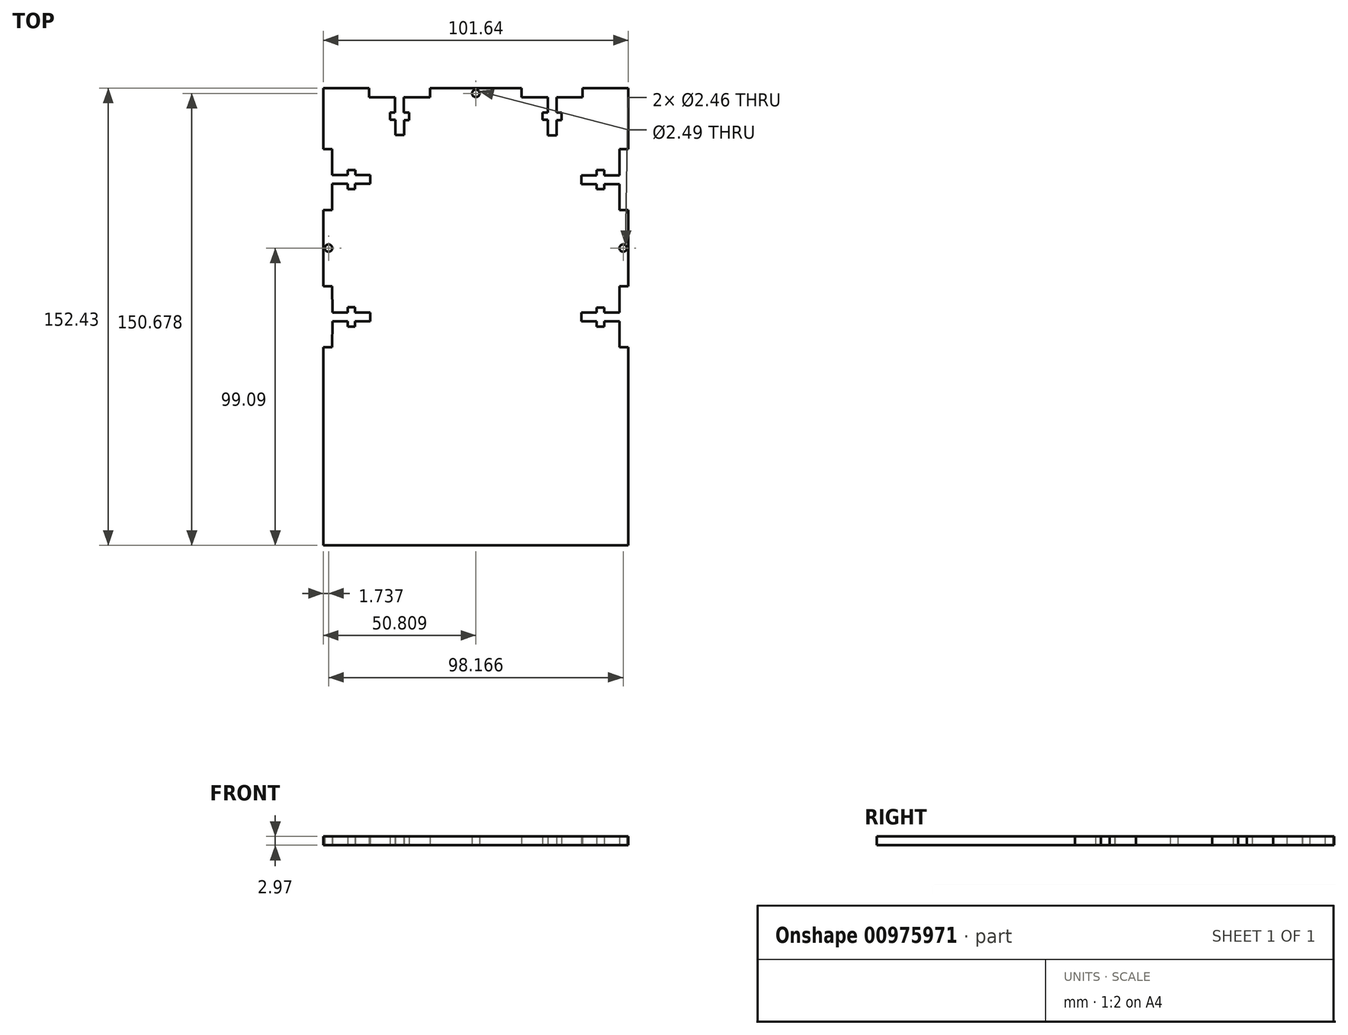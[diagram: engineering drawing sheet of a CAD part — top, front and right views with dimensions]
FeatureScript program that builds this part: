
annotation { "Feature Type Name" : "Feature", "Feature Type Description" : "" }
export const myFeature = defineFeature(function(context is Context, id is Id, definition is map)
    precondition{}
    {
        {
            var Q0;
            Q0=qCreatedBy(makeId("Top.planeOp"),FACE);
            var sketch = newSketch(context, id + "F0", { "sketchPlane" : qUnion([Q0])});
            skLineSegment(sketch, "E0.top", {"start": v(50.82, -76.2) * mm, "end": v(-50.82, -76.2) * mm});
            skPoint(sketch, "E0.middle", {"position": v(0, 0) * mm});
            skPoint(sketch, "E1", {"position": v(-0.02, 76.23) * mm});
            skPoint(sketch, "E2", {"position": v(0, -76.2) * mm});
            skLineSegment(sketch, "E3", {"start": v(-50.82, 76.2) * mm, "end": v(-35.58, 76.2) * mm});
            skLineSegment(sketch, "E4", {"start": v(-0.02, 76.23) * mm, "end": v(-15.26, 76.23) * mm});
            skLineSegment(sketch, "E5", {"start": v(-0.02, 76.23) * mm, "end": v(15.22, 76.23) * mm});
            skLineSegment(sketch, "E6", {"start": v(35.58, 76.2) * mm, "end": v(50.82, 76.2) * mm});
            skLineSegment(sketch, "E7", {"start": v(-50.82, 55.88) * mm, "end": v(-50.82, 76.2) * mm});
            skLineSegment(sketch, "E8", {"start": v(-50.82, 35.56) * mm, "end": v(-50.82, 10.16) * mm});
            skLineSegment(sketch, "E9", {"start": v(-50.82, -10.16) * mm, "end": v(-50.82, -76.2) * mm});
            skLineSegment(sketch, "E10", {"start": v(50.82, -76.2) * mm, "end": v(50.82, -10.16) * mm});
            skLineSegment(sketch, "E11", {"start": v(50.82, 10.16) * mm, "end": v(50.82, 35.56) * mm});
            skLineSegment(sketch, "E12", {"start": v(50.82, 55.88) * mm, "end": v(50.82, 76.2) * mm});
            skLineSegment(sketch, "E13", {"start": v(-50.82, 10.16) * mm, "end": v(-47.85, 10.16) * mm});
            skLineSegment(sketch, "E14", {"start": v(-50.82, -10.16) * mm, "end": v(-47.85, -10.16) * mm});
            skLineSegment(sketch, "E15", {"start": v(-50.82, 55.88) * mm, "end": v(-47.85, 55.88) * mm});
            skLineSegment(sketch, "E16", {"start": v(-50.82, 35.56) * mm, "end": v(-47.85, 35.56) * mm});
            skLineSegment(sketch, "E17", {"start": v(-35.58, 76.2) * mm, "end": v(-35.58, 73.23) * mm});
            skLineSegment(sketch, "E18", {"start": v(-15.26, 76.23) * mm, "end": v(-15.26, 73.23) * mm});
            skLineSegment(sketch, "E19", {"start": v(15.22, 76.23) * mm, "end": v(15.22, 73.23) * mm});
            skLineSegment(sketch, "E20", {"start": v(35.58, 76.2) * mm, "end": v(35.58, 73.23) * mm});
            skLineSegment(sketch, "E21", {"start": v(50.82, 55.88) * mm, "end": v(47.85, 55.88) * mm});
            skLineSegment(sketch, "E22", {"start": v(50.82, 35.56) * mm, "end": v(47.85, 35.56) * mm});
            skLineSegment(sketch, "E23", {"start": v(50.82, 10.16) * mm, "end": v(47.85, 10.16) * mm});
            skLineSegment(sketch, "E24", {"start": v(50.82, -10.16) * mm, "end": v(47.85, -10.16) * mm});
            skLineSegment(sketch, "E25.MirrorCS", {"start": v(-35.15, 45.76) * mm, "end": v(-35.15, 44.3) * mm});
            skLineSegment(sketch, "E26", {"start": v(-47.85, 47.2) * mm, "end": v(-47.85, 55.88) * mm});
            skLineSegment(sketch, "E27", {"start": v(-47.85, 44.3) * mm, "end": v(-47.85, 35.56) * mm});
            skLineSegment(sketch, "E28.bottom", {"start": v(-42.73, 48.94) * mm, "end": v(-40.19, 48.94) * mm});
            skLineSegment(sketch, "E28.top", {"start": v(-42.73, 42.57) * mm, "end": v(-40.26, 42.57) * mm});
            skLineSegment(sketch, "E29", {"start": v(-47.85, 47.2) * mm, "end": v(-42.73, 47.2) * mm});
            skLineSegment(sketch, "E30", {"start": v(-47.85, 44.3) * mm, "end": v(-42.73, 44.3) * mm});
            skLineSegment(sketch, "E31", {"start": v(-35.15, 44.3) * mm, "end": v(-40.26, 44.3) * mm});
            skLineSegment(sketch, "E32", {"start": v(-40.19, 48.94) * mm, "end": v(-40.19, 47.2) * mm});
            skLineSegment(sketch, "E33", {"start": v(-40.26, 44.3) * mm, "end": v(-40.26, 42.57) * mm});
            skLineSegment(sketch, "E34", {"start": v(-42.73, 42.57) * mm, "end": v(-42.73, 44.3) * mm});
            skLineSegment(sketch, "E35", {"start": v(-42.73, 47.2) * mm, "end": v(-42.73, 48.94) * mm});
            skPoint(sketch, "E36", {"position": v(-50.82, 22.86) * mm});
            skLineSegment(sketch, "E37", {"start": v(-25.42, 60.56) * mm, "end": v(-23.96, 60.56) * mm});
            skLineSegment(sketch, "E38.left", {"start": v(-28.6, 68.12) * mm, "end": v(-28.6, 65.66) * mm});
            skLineSegment(sketch, "E38.right", {"start": v(-22.24, 68.12) * mm, "end": v(-22.24, 65.58) * mm});
            skLineSegment(sketch, "E39", {"start": v(-26.88, 73.24) * mm, "end": v(-26.88, 68.12) * mm});
            skLineSegment(sketch, "E40", {"start": v(-23.97, 73.23) * mm, "end": v(-23.97, 68.12) * mm});
            skLineSegment(sketch, "E41", {"start": v(-23.96, 60.56) * mm, "end": v(-23.96, 65.58) * mm});
            skLineSegment(sketch, "E42", {"start": v(-28.6, 68.12) * mm, "end": v(-26.88, 68.12) * mm});
            skLineSegment(sketch, "E43", {"start": v(-23.97, 68.12) * mm, "end": v(-22.24, 68.12) * mm});
            skLineSegment(sketch, "E44", {"start": v(-22.24, 65.58) * mm, "end": v(-23.96, 65.58) * mm});
            skLineSegment(sketch, "E45", {"start": v(-26.88, 65.66) * mm, "end": v(-28.6, 65.66) * mm});
            skLineSegment(sketch, "E46", {"start": v(-35.58, 73.23) * mm, "end": v(-26.88, 73.24) * mm});
            skLineSegment(sketch, "E47", {"start": v(-23.97, 73.23) * mm, "end": v(-15.26, 73.23) * mm});
            skLineSegment(sketch, "E48.MirrorCS", {"start": v(23.92, 68.1) * mm, "end": v(22.2, 68.1) * mm});
            skLineSegment(sketch, "E49.MirrorCS", {"start": v(28.56, 68.12) * mm, "end": v(26.88, 68.12) * mm});
            skLineSegment(sketch, "E50.MirrorCS", {"start": v(26.84, 65.58) * mm, "end": v(28.56, 65.58) * mm});
            skLineSegment(sketch, "E51.MirrorCS", {"start": v(22.2, 65.64) * mm, "end": v(23.92, 65.64) * mm});
            skLineSegment(sketch, "E52.MirrorCS", {"start": v(25.38, 60.53) * mm, "end": v(23.92, 60.53) * mm});
            skLineSegment(sketch, "E53.MirrorCS", {"start": v(23.92, 60.53) * mm, "end": v(23.92, 65.64) * mm});
            skLineSegment(sketch, "E54.MirrorCS", {"start": v(22.2, 68.1) * mm, "end": v(22.2, 65.64) * mm});
            skLineSegment(sketch, "E55.MirrorCS", {"start": v(26.88, 73.24) * mm, "end": v(26.88, 68.12) * mm});
            skLineSegment(sketch, "E56.MirrorCS", {"start": v(23.92, 73.23) * mm, "end": v(23.92, 68.1) * mm});
            skLineSegment(sketch, "E57.MirrorCS", {"start": v(28.56, 68.12) * mm, "end": v(28.56, 65.58) * mm});
            skLineSegment(sketch, "E58", {"start": v(15.22, 73.23) * mm, "end": v(23.92, 73.23) * mm});
            skLineSegment(sketch, "E59", {"start": v(26.88, 73.24) * mm, "end": v(35.58, 73.23) * mm});
            skLineSegment(sketch, "E60.bottom", {"start": v(40.28, 42.59) * mm, "end": v(42.82, 42.59) * mm});
            skLineSegment(sketch, "E60.top", {"start": v(40.28, 48.93) * mm, "end": v(42.74, 48.93) * mm});
            skLineSegment(sketch, "E61", {"start": v(35.15, 44.26) * mm, "end": v(40.28, 44.26) * mm});
            skLineSegment(sketch, "E62", {"start": v(47.85, 44.26) * mm, "end": v(42.82, 44.26) * mm});
            skLineSegment(sketch, "E63", {"start": v(47.85, 47.18) * mm, "end": v(42.74, 47.18) * mm});
            skLineSegment(sketch, "E64", {"start": v(40.28, 47.18) * mm, "end": v(40.28, 48.93) * mm});
            skLineSegment(sketch, "E65", {"start": v(40.28, 44.26) * mm, "end": v(40.28, 42.59) * mm});
            skLineSegment(sketch, "E66", {"start": v(42.82, 42.59) * mm, "end": v(42.82, 44.26) * mm});
            skLineSegment(sketch, "E67", {"start": v(42.74, 47.18) * mm, "end": v(42.74, 48.93) * mm});
            skLineSegment(sketch, "E68", {"start": v(47.85, 47.18) * mm, "end": v(47.85, 55.88) * mm});
            skLineSegment(sketch, "E69", {"start": v(47.85, 44.26) * mm, "end": v(47.85, 35.56) * mm});
            skPoint(sketch, "E70", {"position": v(50.82, 22.86) * mm});
            skLineSegment(sketch, "E71.MirrorCS", {"start": v(42.82, 3.14) * mm, "end": v(42.82, 1.46) * mm});
            skLineSegment(sketch, "E72.MirrorCS", {"start": v(35.15, 0) * mm, "end": v(35.15, 1.46) * mm});
            skLineSegment(sketch, "E73.MirrorCS", {"start": v(40.28, 1.46) * mm, "end": v(40.28, 3.14) * mm});
            skLineSegment(sketch, "E74.MirrorCS", {"start": v(35.15, 0) * mm, "end": v(35.15, -1.46) * mm});
            skLineSegment(sketch, "E75.MirrorCS", {"start": v(40.28, -1.46) * mm, "end": v(40.28, -3.21) * mm});
            skLineSegment(sketch, "E76.MirrorCS", {"start": v(35.15, -1.46) * mm, "end": v(40.28, -1.46) * mm});
            skLineSegment(sketch, "E77.MirrorCS", {"start": v(35.15, 1.46) * mm, "end": v(40.28, 1.46) * mm});
            skLineSegment(sketch, "E78.MirrorCS", {"start": v(40.28, 3.14) * mm, "end": v(42.82, 3.14) * mm});
            skLineSegment(sketch, "E79.MirrorCS", {"start": v(40.28, -3.21) * mm, "end": v(42.74, -3.21) * mm});
            skLineSegment(sketch, "E80.MirrorCS", {"start": v(47.85, -1.46) * mm, "end": v(42.74, -1.46) * mm});
            skLineSegment(sketch, "E81", {"start": v(47.85, 1.46) * mm, "end": v(47.85, 10.16) * mm});
            skLineSegment(sketch, "E82", {"start": v(47.85, -1.46) * mm, "end": v(47.85, -10.16) * mm});
            skLineSegment(sketch, "E83.MirrorCS", {"start": v(-40.26, 1.43) * mm, "end": v(-40.26, 3.16) * mm});
            skLineSegment(sketch, "E84.MirrorCS", {"start": v(-35.15, -0.03) * mm, "end": v(-35.15, 1.43) * mm});
            skLineSegment(sketch, "E85.MirrorCS", {"start": v(-35.15, 1.43) * mm, "end": v(-40.26, 1.43) * mm});
            skLineSegment(sketch, "E86.MirrorCS", {"start": v(-42.72, -1.5) * mm, "end": v(-42.72, -3.22) * mm});
            skLineSegment(sketch, "E87.MirrorCS", {"start": v(-35.15, -0.03) * mm, "end": v(-35.15, -1.5) * mm});
            skLineSegment(sketch, "E88.MirrorCS", {"start": v(-35.15, -1.5) * mm, "end": v(-40.26, -1.5) * mm});
            skLineSegment(sketch, "E89.MirrorCS", {"start": v(-42.72, -3.22) * mm, "end": v(-40.26, -3.22) * mm});
            skLineSegment(sketch, "E90.MirrorCS", {"start": v(-42.72, 3.16) * mm, "end": v(-40.26, 3.16) * mm});
            skLineSegment(sketch, "E91.MirrorCS", {"start": v(-42.72, 3.16) * mm, "end": v(-42.72, 1.43) * mm});
            skLineSegment(sketch, "E92.MirrorCS", {"start": v(-40.26, -3.22) * mm, "end": v(-40.26, -1.5) * mm});
            skPoint(sketch, "E93", {"position": v(-47.85, 22.86) * mm});
            skCircle(sketch, "E94", {"center": v(-49.08, 22.9) * mm, "radius": 1.23 * mm});
            skPoint(sketch, "E94.third.point", {"position": v(-50.31, 22.92) * mm});
            skCircle(sketch, "E95.MirrorC", {"center": v(49.08, 22.9) * mm, "radius": 1.23 * mm});
            skCircle(sketch, "E96", {"center": v(-0.01, 74.48) * mm, "radius": 1.25 * mm});
            skPoint(sketch, "E96.first.point", {"position": v(-0.02, 73.23) * mm});
            skPoint(sketch, "E96.third.point", {"position": v(0, 75.72) * mm});
            skLineSegment(sketch, "E97", {"start": v(25.38, 60.53) * mm, "end": v(26.84, 60.53) * mm});
            skLineSegment(sketch, "E98", {"start": v(26.84, 60.53) * mm, "end": v(26.84, 65.58) * mm});
            skLineSegment(sketch, "E99", {"start": v(-25.42, 60.56) * mm, "end": v(-26.88, 60.56) * mm});
            skLineSegment(sketch, "E100", {"start": v(-26.88, 60.56) * mm, "end": v(-26.88, 65.66) * mm});
            skPoint(sketch, "E101", {"position": v(-47.82, -1.5) * mm});
            skLineSegment(sketch, "E102", {"start": v(-47.85, -10.16) * mm, "end": v(-47.82, -1.5) * mm});
            skLineSegment(sketch, "E103", {"start": v(-47.82, -1.5) * mm, "end": v(-42.72, -1.5) * mm});
            skPoint(sketch, "E104", {"position": v(-47.82, 1.43) * mm});
            skLineSegment(sketch, "E105", {"start": v(-42.72, 1.43) * mm, "end": v(-47.82, 1.43) * mm});
            skLineSegment(sketch, "E106", {"start": v(42.82, 1.46) * mm, "end": v(47.85, 1.46) * mm});
            skLineSegment(sketch, "E107", {"start": v(-35.15, 45.76) * mm, "end": v(-35.15, 47.2) * mm});
            skLineSegment(sketch, "E108", {"start": v(-35.15, 47.2) * mm, "end": v(-40.19, 47.2) * mm});
            skLineSegment(sketch, "E109", {"start": v(40.28, 47.18) * mm, "end": v(35.15, 47.18) * mm});
            skLineSegment(sketch, "E110", {"start": v(35.15, 47.18) * mm, "end": v(35.15, 44.26) * mm});
            skLineSegment(sketch, "E111", {"start": v(-47.85, 10.16) * mm, "end": v(-47.82, 1.43) * mm});
            skLineSegment(sketch, "E112", {"start": v(47.85, -4.6) * mm, "end": v(47.85, -1.46) * mm});
            skLineSegment(sketch, "E113", {"start": v(42.74, -1.46) * mm, "end": v(42.74, -3.21) * mm});
            skSolve(sketch);
        }
        {
            var Q0;
            Q0=makeQuery(id+"F0.imprint","IMPRINT",FACE,{"disambiguationData":[TD([[makeQuery(id+"F0.imprint","IMPRINT",EDGE,{"derivedFrom":sQuery(id+"F0.wireOp",EDGE,"E0.top")}),-1.0]])]});
            extrude(context, id + "F1", {"entities" : qUnion([Q0]), "depth" : 2.97 * mm, "offsetDistance" : 25.4 * mm});
        }
    });
